# Revit family: EDLR-235-3000-xxx-SMTx
name_source: partatom
category: Leuchten
revit_build: Autodesk Revit 2017 (Build: 20190508_0315(x64)
units: mm (PartAtom-declared; Revit-internal decimal feet)

## family parameters
Basisbauteil = Fläche
Beim Laden mit Abzugskörper schneiden = Ja
Bemaßung runder Anschluss = Durchmesser verwenden
Gemeinsam genutzt = Nein
Lichtquelle = Ja
OmniClass-Nummer = 23.80.70.11
OmniClass-Titel = Luminaries for Internal Lighting
Raumberechnungspunkt = Nein
Teiletyp = Normal

## types (4) — shared parameters
Baugruppenkennzeichen = D5020200
Datei für fotometrisches Netz = EDLR 235_3000-840 SMT.IES
Emissionsform beim Rendern sichtbar = Nein
Farbfilter = 16777215
Farbtemperaturverschiebung bei Dämpfen der Lampe = <Keine Auswahl>
Hersteller = RIDI Leuchten GmbH
Lampe = LED
Neigungswinkel = 90.00°
Scheinlast = 23 VA
URL = www.ridi.de
Von Kreisdurchmesser aussenden = 210 mm  [stored 0.688976 ft]
brand = RIDI
conformity mark = CE
electrical safety class = 1
height = 60 mm  [stored 0.19685 ft]
ingress protection (IP) code = IP20
length = 235 mm  [stored 0.770997 ft]
nominal frequency = 50-60Hz
nominal voltage = 230
rated input power = 23
voltage type (AC, DC, UC) = AC
weight = 1.2 kg
width = 235 mm  [stored 0.770997 ft]
zero-valued in all types: Vorgabe-Ansicht

## per-type parameters (varying)
| type | Modell | product name |
| EDLR 235/3000-830 SMT | 0321332 | EDLR 235/3000-830 SMT |
| EDLR 235/3000-830 SMT-DALI | 0331332 | EDLR 235/3000-830 SMT |
| EDLR 235/3000-840 SMT | 0321331 | EDLR 235/3000-840 SMT |
| EDLR 235/3000-840 SMT-DALI | 0331331 | EDLR 235/3000-840 SMT-DALI |

note: [stored X ft] marks values corroborated as IEEE doubles in the binary element streams (Revit-internal decimal feet)
